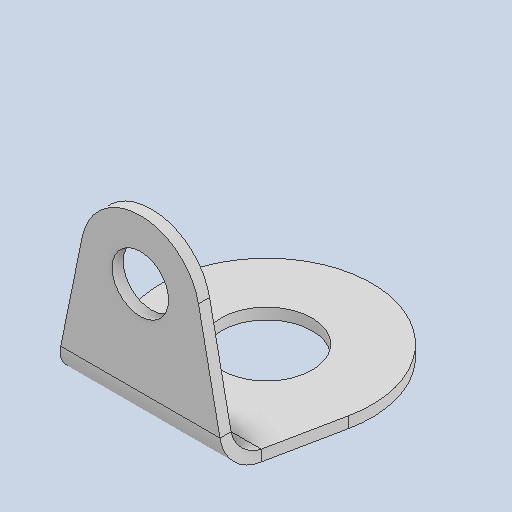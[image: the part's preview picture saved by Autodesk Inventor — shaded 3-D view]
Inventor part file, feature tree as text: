
AUTODESK INVENTOR PART (.ipt)
format: ipt  version: 2024.2 (Build 282272000, 272)  size: 104,448 bytes
history: native  units: in
note: dims shown in document units (in); Inventor stores cm internally (conversion verified against a paired STEP export)
features: sketch x1
ambient origin geometry x8: Origin, YZ Plane, XZ Plane, XY Plane, X Axis, Y Axis, Z Axis, Center Point
bodies: Solid1 (feature_tree)
feature tree (1):
  sketch  "Sketched Bend2"
